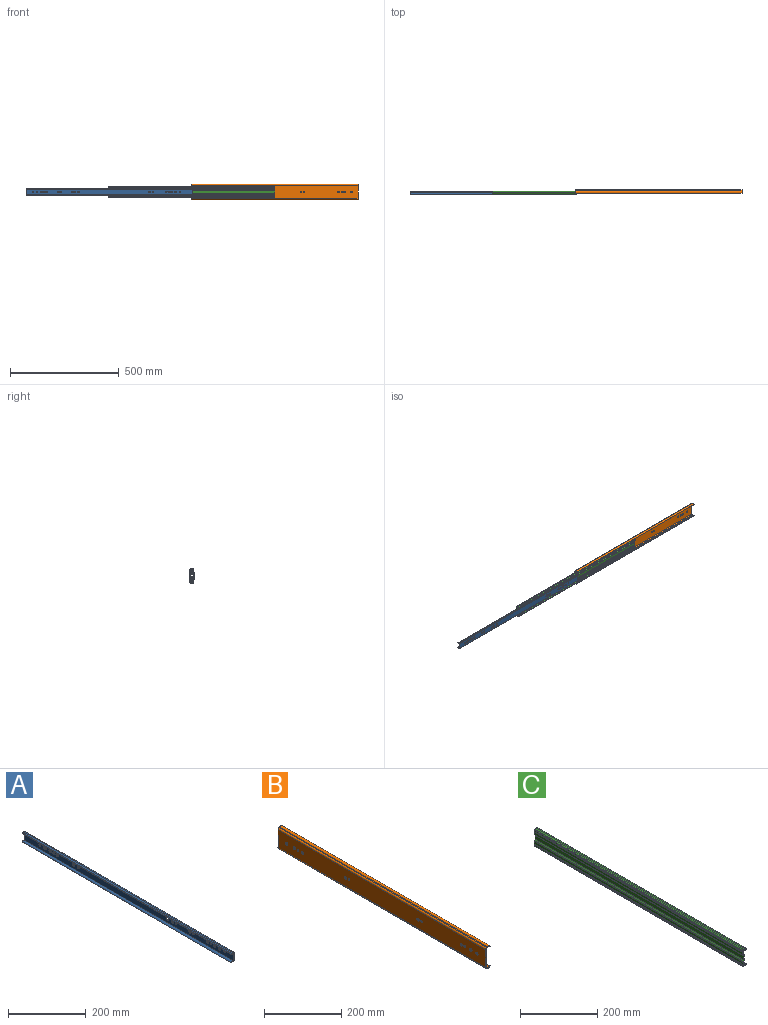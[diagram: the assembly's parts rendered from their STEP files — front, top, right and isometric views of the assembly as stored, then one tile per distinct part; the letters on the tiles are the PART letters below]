
ASSEMBLY  parts=3 mates=2
PART A: 31 faces, bbox 11x762x30.6 mm
  f0: cylinder r=4mm len=762mm, axis (0,1,0), area 4893.3mm2, adj f1,f11,f12,f13
  f1: plane 762x1.44mm, normal (-0.69,0,0.72), area 1524mm2, adj f0,f2,f12,f13
  f2: cylinder r=6mm len=762mm, axis (0,1,0), area 7339.9mm2, adj f1,f3,f12,f13
  f3: cylinder r=0.19mm len=762mm, axis (0,1,0), area 352.6mm2, adj f2,f4,f12,f13
  f4: plane 762x26.19mm, normal (-1,0,0), area 19156.3mm2, adj f3,f5,f12,f13,f14,f15,f16,f17
  f5: cylinder r=0.19mm len=762mm, axis (0,1,0), area 352.6mm2, adj f4,f6,f12,f13
  f6: cylinder r=6mm len=762mm, axis (0,1,0), area 7339.9mm2, adj f5,f7,f12,f13
  f7: plane 762x1.44mm, normal (-0.69,0,-0.72), area 1524mm2, adj f6,f8,f12,f13
  f8: cylinder r=4mm len=762mm, axis (0,1,0), area 4893.3mm2, adj f7,f9,f12,f13
  f9: cylinder r=2.19mm len=762mm, axis (0,1,0), area 3969.8mm2, adj f8,f10,f12,f13
  f10: plane 762x26.19mm, normal (1,0,0), area 19156.3mm2, adj f9,f11,f12,f13,f14,f15,f16,f17
  f11: cylinder r=2.19mm len=762mm, axis (0,1,0), area 3969.8mm2, adj f0,f10,f12,f13
  f12: plane 30.58x10.97mm, normal (0,-1,0), area 95.8mm2, adj f0,f1,f2,f3,f4,f5,f6,f7
  f13: plane 30.58x10.97mm, normal (0,1,0), area 95.8mm2, adj f0,f1,f2,f3,f4,f5,f6,f7
  f14: cylinder r=4.25mm len=8.5mm, axis (-1,0,0), area 53.4mm2, adj f4,f10
  f15: cylinder r=4.25mm len=8.5mm, axis (-1,0,0), area 53.4mm2, adj f4,f10
  f16: cylinder r=2.95mm len=5.9mm, axis (-1,0,0), area 37.1mm2, adj f4,f10
  f17: cylinder r=4.25mm len=8.5mm, axis (-1,0,0), area 53.4mm2, adj f4,f10
  f18: cylinder r=2.95mm len=5.9mm, axis (-1,0,0), area 37.1mm2, adj f4,f10
  f19: cylinder r=4.25mm len=8.5mm, axis (-1,0,0), area 53.4mm2, adj f4,f10
  f20: cylinder r=4.5mm len=9mm, axis (-1,0,0), area 56.5mm2, adj f4,f10
  f21: cylinder r=4.5mm len=9mm, axis (-1,0,0), area 56.5mm2, adj f4,f10
  f22: cylinder r=2.95mm len=5.9mm, axis (-1,0,0), area 37.1mm2, adj f4,f10
  f23: cylinder r=4.25mm len=8.5mm, axis (-1,0,0), area 53.4mm2, adj f4,f10
  f24: cylinder r=2.95mm len=5.9mm, axis (-1,0,0), area 37.1mm2, adj f4,f10
  f25: cylinder r=4.25mm len=8.5mm, axis (-1,0,0), area 53.4mm2, adj f4,f10
  f26: cylinder r=4.25mm len=8.5mm, axis (-1,0,0), area 53.4mm2, adj f4,f10
  f27: cylinder r=2.95mm len=5.9mm, axis (-1,0,0), area 37.1mm2, adj f4,f10
  f28: cylinder r=4.25mm len=8.5mm, axis (-1,0,0), area 53.4mm2, adj f4,f10
  f29: cylinder r=4.25mm len=8.5mm, axis (-1,0,0), area 53.4mm2, adj f4,f10
  f30: cylinder r=2.95mm len=5.9mm, axis (-1,0,0), area 37.1mm2, adj f4,f10
PART B: 30 faces, bbox 16.3x762x70.8 mm
  f0: cylinder r=4mm len=762mm, axis (0,1,0), area 6008.8mm2, adj f1,f15,f16,f17
  f1: plane 762x1.86mm, normal (0.37,0,-0.93), area 1524mm2, adj f0,f2,f16,f17
  f2: cylinder r=6mm len=762mm, axis (0,1,0), area 9013.1mm2, adj f1,f3,f16,f17
  f3: cylinder r=2.62mm len=762mm, axis (0,1,0), area 1562.8mm2, adj f2,f4,f16,f17
  f4: cylinder r=4.62mm len=762mm, axis (0,1,0), area 5530.3mm2, adj f3,f5,f16,f17
  f5: plane 762x56.54mm, normal (-1,0,0), area 42522mm2, adj f4,f6,f16,f17,f18,f19,f20,f21
  f6: cylinder r=4.62mm len=762mm, axis (0,1,0), area 5530.3mm2, adj f5,f7,f16,f17
  f7: cylinder r=2.62mm len=762mm, axis (0,1,0), area 1562.8mm2, adj f6,f8,f16,f17
  f8: cylinder r=6mm len=762mm, axis (0,1,0), area 9013.1mm2, adj f7,f9,f16,f17
  f9: plane 762x1.86mm, normal (0.37,0,0.93), area 1524mm2, adj f8,f10,f16,f17
  f10: cylinder r=4mm len=762mm, axis (0,1,0), area 6008.8mm2, adj f9,f11,f16,f17
  f11: cylinder r=4.62mm len=762mm, axis (0,1,0), area 2755.7mm2, adj f10,f12,f16,f17
  f12: cylinder r=2.62mm len=762mm, axis (0,1,0), area 3136.4mm2, adj f11,f13,f16,f17
  f13: plane 762x56.54mm, normal (1,0,0), area 42522mm2, adj f12,f14,f16,f17,f18,f19,f20,f21
  f14: cylinder r=2.62mm len=762mm, axis (0,1,0), area 3136.4mm2, adj f13,f15,f16,f17
  f15: cylinder r=4.62mm len=762mm, axis (0,1,0), area 2755.7mm2, adj f0,f14,f16,f17
  f16: plane 70.8x16.27mm, normal (0,-1,0), area 186.6mm2, adj f0,f1,f2,f3,f4,f5,f6,f7
  f17: plane 70.8x16.27mm, normal (0,1,0), area 186.6mm2, adj f0,f1,f2,f3,f4,f5,f6,f7
  f18: cylinder r=4.25mm len=8.5mm, axis (-1,0,0), area 53.4mm2, adj f5,f13
  f19: cylinder r=4.25mm len=8.5mm, axis (-1,0,0), area 53.4mm2, adj f5,f13
  f20: cylinder r=2.95mm len=5.9mm, axis (-1,0,0), area 37.1mm2, adj f5,f13
  f21: cylinder r=4.25mm len=8.5mm, axis (-1,0,0), area 53.4mm2, adj f5,f13
  f22: cylinder r=4.25mm len=8.5mm, axis (-1,0,0), area 53.4mm2, adj f5,f13
  f23: cylinder r=2.95mm len=5.9mm, axis (-1,0,0), area 37.1mm2, adj f5,f13
  f24: cylinder r=4.25mm len=8.5mm, axis (-1,0,0), area 53.4mm2, adj f5,f13
  f25: cylinder r=2.95mm len=5.9mm, axis (-1,0,0), area 37.1mm2, adj f5,f13
  f26: cylinder r=4.25mm len=8.5mm, axis (-1,0,0), area 53.4mm2, adj f5,f13
  f27: cylinder r=2.95mm len=5.9mm, axis (-1,0,0), area 37.1mm2, adj f5,f13
  f28: cylinder r=4.25mm len=8.5mm, axis (-1,0,0), area 53.4mm2, adj f5,f13
  f29: cylinder r=4.25mm len=8.5mm, axis (-1,0,0), area 53.4mm2, adj f5,f13
PART C: 58 faces, bbox 12.4x762x54.7 mm
  f0: cylinder r=2.19mm len=762mm, axis (0,1,0), area 3989.4mm2, adj f1,f55,f56,f57
  f1: plane 762x2.2mm, normal (1,0,0), area 1676.4mm2, adj f0,f2,f56,f57
  f2: cylinder r=2.19mm len=762mm, axis (0,1,0), area 3398.2mm2, adj f1,f3,f56,f57
  f3: cylinder r=4mm len=762mm, axis (0,1,0), area 4491.3mm2, adj f2,f4,f56,f57
  f4: cylinder r=2.19mm len=762mm, axis (0,1,0), area 1693.5mm2, adj f3,f5,f56,f57
  f5: cylinder r=0.19mm len=762mm, axis (0,1,0), area 233.3mm2, adj f4,f6,f56,f57
  f6: plane 762x7.5mm, normal (1,0,0), area 5715mm2, adj f5,f7,f56,f57
  f7: cylinder r=0.19mm len=762mm, axis (0,1,0), area 128.8mm2, adj f6,f8,f56,f57
  f8: plane 762x3.16mm, normal (0.65,0,-0.76), area 3153.9mm2, adj f7,f9,f56,f57
  f9: cylinder r=2.19mm len=762mm, axis (0,1,0), area 1450.5mm2, adj f8,f10,f56,f57
  f10: plane 762x12.58mm, normal (1,0,0), area 9588.3mm2, adj f9,f11,f56,f57
  f11: cylinder r=2.19mm len=762mm, axis (0,1,0), area 1450.5mm2, adj f10,f12,f56,f57
  f12: plane 762x3.16mm, normal (0.65,0,0.76), area 3153.9mm2, adj f11,f13,f56,f57
  f13: cylinder r=0.19mm len=762mm, axis (0,1,0), area 128.8mm2, adj f12,f14,f56,f57
  f14: plane 762x7.5mm, normal (1,0,0), area 5715mm2, adj f13,f15,f56,f57
  f15: cylinder r=0.19mm len=762mm, axis (0,1,0), area 233.3mm2, adj f14,f16,f56,f57
  f16: cylinder r=2.19mm len=762mm, axis (0,1,0), area 1693.5mm2, adj f15,f17,f56,f57
  f17: cylinder r=4mm len=762mm, axis (0,1,0), area 4491.3mm2, adj f16,f18,f56,f57
  f18: cylinder r=2.19mm len=762mm, axis (0,1,0), area 3398.2mm2, adj f17,f19,f56,f57
  f19: plane 762x2.2mm, normal (1,0,0), area 1676.4mm2, adj f18,f20,f56,f57
  f20: cylinder r=2.19mm len=762mm, axis (0,1,0), area 3989.4mm2, adj f19,f21,f56,f57
  f21: cylinder r=4mm len=762mm, axis (0,1,0), area 4315mm2, adj f20,f22,f56,f57
  f22: cylinder r=2.19mm len=762mm, axis (0,1,0), area 3632.9mm2, adj f21,f23,f56,f57
  f23: plane 762x3mm, normal (-1,0,0), area 2286mm2, adj f22,f24,f56,f57
  f24: plane 762x2mm, normal (0,0,-1), area 1524mm2, adj f23,f25,f56,f57
  f25: plane 762x3mm, normal (1,0,0), area 2286mm2, adj f24,f26,f56,f57
  f26: cylinder r=0.19mm len=762mm, axis (0,1,0), area 322.7mm2, adj f25,f27,f56,f57
  f27: cylinder r=6mm len=762mm, axis (0,1,0), area 6472.4mm2, adj f26,f28,f56,f57
  f28: cylinder r=0.19mm len=762mm, axis (0,1,0), area 354.3mm2, adj f27,f29,f56,f57
  f29: plane 762x2.2mm, normal (-1,0,0), area 1676.4mm2, adj f28,f30,f56,f57
  f30: cylinder r=0.19mm len=762mm, axis (0,1,0), area 301.8mm2, adj f29,f31,f56,f57
  f31: cylinder r=6mm len=762mm, axis (0,1,0), area 6736.9mm2, adj f30,f32,f56,f57
  f32: cylinder r=0.19mm len=762mm, axis (0,1,0), area 150.4mm2, adj f31,f33,f56,f57
  f33: cylinder r=2.19mm len=762mm, axis (0,1,0), area 2627.2mm2, adj f32,f34,f56,f57
  f34: plane 762x7.5mm, normal (-1,0,0), area 5715mm2, adj f33,f35,f56,f57
  f35: cylinder r=2.19mm len=762mm, axis (0,1,0), area 1450.5mm2, adj f34,f36,f56,f57
  f36: plane 762x3.16mm, normal (-0.65,0,-0.76), area 3153.9mm2, adj f35,f37,f56,f57
  f37: cylinder r=0.19mm len=762mm, axis (0,1,0), area 128.8mm2, adj f36,f38,f56,f57
  f38: plane 762x12.58mm, normal (-1,0,0), area 9588.3mm2, adj f37,f39,f56,f57
  f39: cylinder r=0.19mm len=762mm, axis (0,1,0), area 128.8mm2, adj f38,f40,f56,f57
  f40: plane 762x3.16mm, normal (-0.65,0,0.76), area 3153.9mm2, adj f39,f41,f56,f57
  f41: cylinder r=2.19mm len=762mm, axis (0,1,0), area 1450.5mm2, adj f40,f42,f56,f57
  f42: plane 762x7.5mm, normal (-1,0,0), area 5715mm2, adj f41,f43,f56,f57
  f43: cylinder r=2.19mm len=762mm, axis (0,1,0), area 2627.2mm2, adj f42,f44,f56,f57
  f44: cylinder r=0.19mm len=762mm, axis (0,1,0), area 150.4mm2, adj f43,f45,f56,f57
  f45: cylinder r=6mm len=762mm, axis (0,1,0), area 6736.9mm2, adj f44,f46,f56,f57
  f46: cylinder r=0.19mm len=762mm, axis (0,1,0), area 301.8mm2, adj f45,f47,f56,f57
  f47: plane 762x2.2mm, normal (-1,0,0), area 1676.4mm2, adj f46,f48,f56,f57
  f48: cylinder r=0.19mm len=762mm, axis (0,1,0), area 354.3mm2, adj f47,f49,f56,f57
  f49: cylinder r=6mm len=762mm, axis (0,1,0), area 6472.4mm2, adj f48,f50,f56,f57
  f50: cylinder r=0.19mm len=762mm, axis (0,1,0), area 322.7mm2, adj f49,f51,f56,f57
  f51: plane 762x3mm, normal (1,0,0), area 2286mm2, adj f50,f52,f56,f57
  f52: plane 762x2mm, normal (0,0,1), area 1524mm2, adj f51,f53,f56,f57
  f53: plane 762x3mm, normal (-1,0,0), area 2286mm2, adj f52,f54,f56,f57
  f54: cylinder r=2.19mm len=762mm, axis (0,1,0), area 3632.9mm2, adj f53,f55,f56,f57
  f55: cylinder r=4mm len=762mm, axis (0,1,0), area 4315mm2, adj f0,f54,f56,f57
  f56: plane 54.69x12.4mm, normal (0,-1,0), area 202.4mm2, adj f0,f1,f2,f3,f4,f5,f6,f7
  f57: plane 54.69x12.4mm, normal (0,1,0), area 202.4mm2, adj f0,f1,f2,f3,f4,f5,f6,f7
PLACE A rot(axis=(0,0,-1),90deg) t=(-381.02,0,0)mm
PLACE B rot(axis=(0,0,-1),90deg) t=(380.98,0,0)mm
PLACE C rot(axis=(0,0,-1),90deg) t=(-0.02,0,0)mm
MATE slider C.f21 <-> B.f0  axis (-1,0,0) through (-762.02,-10.7,29.4)mm
MATE slider A.f0 <-> C.f17  axis (-1,0,0) through (-1143.02,-12.45,17.4)mm
